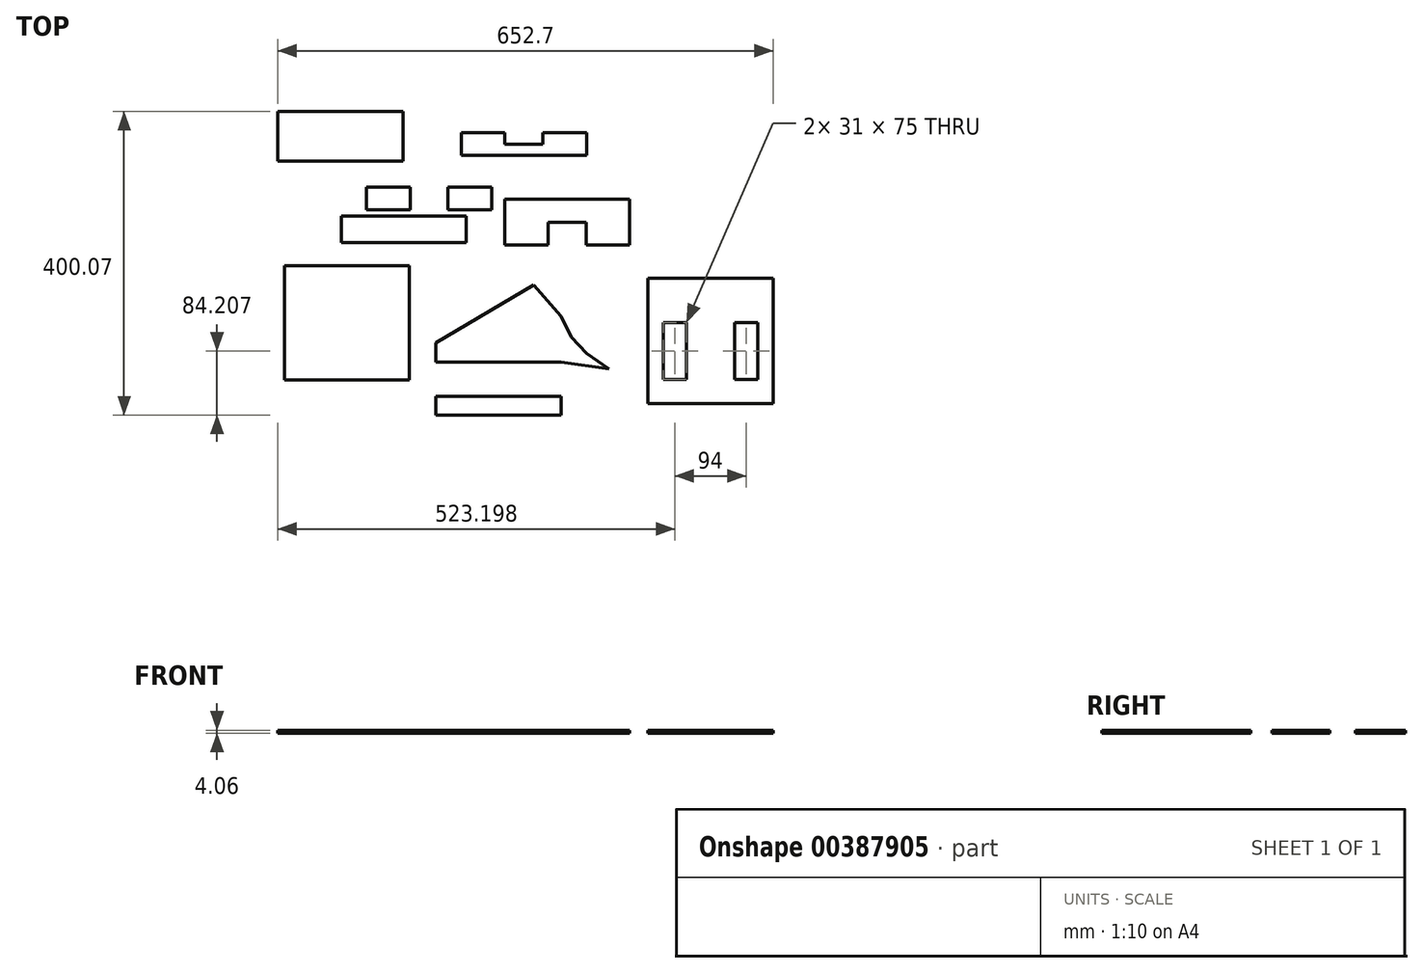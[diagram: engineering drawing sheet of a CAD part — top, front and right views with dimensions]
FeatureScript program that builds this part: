
annotation { "Feature Type Name" : "Feature", "Feature Type Description" : "" }
export const myFeature = defineFeature(function(context is Context, id is Id, definition is map)
    precondition{}
    {
        {
            var Q0;
            Q0=qCreatedBy(makeId("Top.planeOp"),FACE);
            var sketch = newSketch(context, id + "F0", { "sketchPlane" : qUnion([Q0])});
            skLineSegment(sketch, "E0", {"start": v(88.78, 74.8) * mm, "end": v(124.8, 33.23) * mm});
            skLineSegment(sketch, "E1", {"start": v(124.8, 33.23) * mm, "end": v(124.8, -26.77) * mm});
            skLineSegment(sketch, "E2", {"start": v(124.8, -26.77) * mm, "end": v(-40.2, -26.77) * mm});
            skLineSegment(sketch, "E3", {"start": v(88.78, 74.8) * mm, "end": v(-40.2, -1.77) * mm});
            skLineSegment(sketch, "E4", {"start": v(-40.2, -1.77) * mm, "end": v(-40.2, -26.77) * mm});
            skLineSegment(sketch, "E5", {"start": v(124.8, -26.77) * mm, "end": v(187.44, -35.47) * mm});
            skLineSegment(sketch, "E6.bottom", {"start": v(-40.2, -71.68) * mm, "end": v(124.8, -71.68) * mm});
            skLineSegment(sketch, "E6.top", {"start": v(-40.2, -96.68) * mm, "end": v(124.8, -96.68) * mm});
            skLineSegment(sketch, "E6.left", {"start": v(-40.2, -71.68) * mm, "end": v(-40.2, -96.68) * mm});
            skLineSegment(sketch, "E6.right", {"start": v(124.8, -71.68) * mm, "end": v(124.8, -96.68) * mm});
            skLineSegment(sketch, "E7.bottom", {"start": v(-239.93, 99.9) * mm, "end": v(-74.93, 99.9) * mm});
            skLineSegment(sketch, "E7.top", {"start": v(-239.93, -50.1) * mm, "end": v(-74.93, -50.1) * mm});
            skLineSegment(sketch, "E7.left", {"start": v(-239.93, 99.9) * mm, "end": v(-239.93, -50.1) * mm});
            skLineSegment(sketch, "E7.right", {"start": v(-74.93, 99.9) * mm, "end": v(-74.93, -50.1) * mm});
            skLineSegment(sketch, "E8.bottom", {"start": v(239.23, 83.7) * mm, "end": v(404.23, 83.7) * mm});
            skLineSegment(sketch, "E8.top", {"start": v(239.23, -81.3) * mm, "end": v(404.23, -81.3) * mm});
            skLineSegment(sketch, "E8.left", {"start": v(239.23, 83.7) * mm, "end": v(239.23, -81.3) * mm});
            skLineSegment(sketch, "E8.right", {"start": v(404.23, 83.7) * mm, "end": v(404.23, -81.3) * mm});
            skLineSegment(sketch, "E9", {"start": v(124.8, 33.23) * mm, "end": v(138.08, 6.33) * mm});
            skLineSegment(sketch, "E10", {"start": v(138.08, 6.33) * mm, "end": v(158.76, -15.4) * mm});
            skLineSegment(sketch, "E11", {"start": v(158.76, -15.4) * mm, "end": v(187.44, -35.47) * mm});
            skLineSegment(sketch, "E12.bottom", {"start": v(-131.68, 203.81) * mm, "end": v(33.32, 203.81) * mm});
            skLineSegment(sketch, "E12.top", {"start": v(-131.68, 173.81) * mm, "end": v(33.32, 173.81) * mm});
            skLineSegment(sketch, "E12.left", {"start": v(-131.68, 203.81) * mm, "end": v(-131.68, 173.81) * mm});
            skLineSegment(sketch, "E12.right", {"start": v(33.32, 203.81) * mm, "end": v(33.32, 173.81) * mm});
            skLineSegment(sketch, "E13.bottom", {"start": v(-165, 165.7) * mm, "end": v(0, 165.7) * mm});
            skLineSegment(sketch, "E13.top", {"start": v(-165, 130.7) * mm, "end": v(0, 130.7) * mm});
            skLineSegment(sketch, "E13.left", {"start": v(-165, 165.7) * mm, "end": v(-165, 130.7) * mm});
            skLineSegment(sketch, "E13.right", {"start": v(0, 165.7) * mm, "end": v(0, 130.7) * mm});
            skLineSegment(sketch, "E14.bottom", {"start": v(50.31, 187.48) * mm, "end": v(215.31, 187.48) * mm});
            skLineSegment(sketch, "E14.top", {"start": v(50.31, 127.48) * mm, "end": v(215.31, 127.48) * mm});
            skLineSegment(sketch, "E14.left", {"start": v(50.31, 187.48) * mm, "end": v(50.31, 127.48) * mm});
            skLineSegment(sketch, "E14.right", {"start": v(215.31, 187.48) * mm, "end": v(215.31, 127.48) * mm});
            skLineSegment(sketch, "E15.bottom", {"start": v(259.23, 25.03) * mm, "end": v(290.23, 25.03) * mm});
            skLineSegment(sketch, "E15.top", {"start": v(259.23, -49.97) * mm, "end": v(290.23, -49.97) * mm});
            skLineSegment(sketch, "E15.left", {"start": v(259.23, 25.03) * mm, "end": v(259.23, -49.97) * mm});
            skLineSegment(sketch, "E15.right", {"start": v(290.23, 25.03) * mm, "end": v(290.23, -49.97) * mm});
            skLineSegment(sketch, "E16", {"start": v(321.73, 83.7) * mm, "end": v(321.73, -81.3) * mm});
            skLineSegment(sketch, "E17.MirrorCS", {"start": v(384.23, 25.03) * mm, "end": v(353.23, 25.03) * mm});
            skLineSegment(sketch, "E18.MirrorCS", {"start": v(384.23, 25.03) * mm, "end": v(384.23, -49.97) * mm});
            skLineSegment(sketch, "E19.MirrorCS", {"start": v(353.23, 25.03) * mm, "end": v(353.23, -49.97) * mm});
            skLineSegment(sketch, "E20.MirrorCS", {"start": v(384.23, -49.97) * mm, "end": v(353.23, -49.97) * mm});
            skLineSegment(sketch, "E21.bottom", {"start": v(-248.47, 303.39) * mm, "end": v(-83.47, 303.39) * mm});
            skLineSegment(sketch, "E21.top", {"start": v(-248.47, 237.68) * mm, "end": v(-83.47, 237.68) * mm});
            skLineSegment(sketch, "E21.left", {"start": v(-248.47, 303.39) * mm, "end": v(-248.47, 237.68) * mm});
            skLineSegment(sketch, "E21.right", {"start": v(-83.47, 303.39) * mm, "end": v(-83.47, 237.68) * mm});
            skLineSegment(sketch, "E22", {"start": v(-49.18, 173.81) * mm, "end": v(-49.18, 193.81) * mm});
            skLineSegment(sketch, "E23", {"start": v(-49.18, 193.81) * mm, "end": v(-24.18, 193.81) * mm});
            skLineSegment(sketch, "E24", {"start": v(-24.18, 193.81) * mm, "end": v(-24.18, 173.81) * mm});
            skLineSegment(sketch, "E25.MirrorCS", {"start": v(-49.18, 193.81) * mm, "end": v(-74.18, 193.81) * mm});
            skLineSegment(sketch, "E26.MirrorCS", {"start": v(-74.18, 193.81) * mm, "end": v(-74.18, 173.81) * mm});
            skLineSegment(sketch, "E27", {"start": v(-82.5, 165.7) * mm, "end": v(-82.5, 130.7) * mm});
            skLineSegment(sketch, "E28", {"start": v(-107.5, 165.7) * mm, "end": v(-107.5, 150.7) * mm});
            skLineSegment(sketch, "E29", {"start": v(-107.5, 150.7) * mm, "end": v(-82.5, 150.7) * mm});
            skLineSegment(sketch, "E30.MirrorCS", {"start": v(-57.5, 150.7) * mm, "end": v(-82.5, 150.7) * mm});
            skLineSegment(sketch, "E31.MirrorCS", {"start": v(-57.5, 165.7) * mm, "end": v(-57.5, 150.7) * mm});
            skLineSegment(sketch, "E32.bottom", {"start": v(-6.75, 275.29) * mm, "end": v(158.25, 275.29) * mm});
            skLineSegment(sketch, "E32.top", {"start": v(-6.75, 245.29) * mm, "end": v(158.25, 245.29) * mm});
            skLineSegment(sketch, "E32.left", {"start": v(-6.75, 275.29) * mm, "end": v(-6.75, 245.29) * mm});
            skLineSegment(sketch, "E32.right", {"start": v(158.25, 275.29) * mm, "end": v(158.25, 245.29) * mm});
            skLineSegment(sketch, "E33", {"start": v(75.75, 245.29) * mm, "end": v(75.75, 275.29) * mm});
            skLineSegment(sketch, "E34", {"start": v(50.75, 245.29) * mm, "end": v(50.75, 275.29) * mm});
            skLineSegment(sketch, "E35.MirrorCS", {"start": v(100.75, 245.29) * mm, "end": v(100.75, 275.29) * mm});
            skLineSegment(sketch, "E36", {"start": v(-74.18, 193.81) * mm, "end": v(-74.18, 203.81) * mm});
            skLineSegment(sketch, "E37", {"start": v(-49.18, 193.81) * mm, "end": v(-49.18, 203.81) * mm});
            skLineSegment(sketch, "E38", {"start": v(-24.18, 193.81) * mm, "end": v(-24.18, 203.81) * mm});
            skLineSegment(sketch, "E39", {"start": v(132.81, 127.48) * mm, "end": v(132.81, 187.48) * mm});
            skLineSegment(sketch, "E40", {"start": v(132.81, 157.48) * mm, "end": v(157.81, 157.48) * mm});
            skLineSegment(sketch, "E41", {"start": v(157.81, 157.48) * mm, "end": v(157.81, 127.48) * mm});
            skLineSegment(sketch, "E42.MirrorCS", {"start": v(132.81, 157.48) * mm, "end": v(107.81, 157.48) * mm});
            skLineSegment(sketch, "E43.MirrorCS", {"start": v(107.81, 157.48) * mm, "end": v(107.81, 127.48) * mm});
            skLineSegment(sketch, "E44", {"start": v(50.75, 260.29) * mm, "end": v(100.75, 260.29) * mm});
            skSolve(sketch);
        }
        {
            var Q0;
            Q0=makeQuery(id+"F0.imprint","IMPRINT",FACE,{"disambiguationData":[TD([[makeQuery(id+"F0.imprint","IMPRINT",EDGE,{"derivedFrom":sQuery(id+"F0.wireOp",EDGE,"E0")}),-1.0]])]});
            var Q1;
            Q1=makeQuery(id+"F0.imprint","IMPRINT",FACE,{"disambiguationData":[TD([[makeQuery(id+"F0.imprint","IMPRINT",EDGE,{"derivedFrom":sQuery(id+"F0.wireOp",EDGE,"E6.bottom")}),-1.0]])]});
            var Q2;
            Q2=makeQuery(id+"F0.imprint","IMPRINT",FACE,{"disambiguationData":[TD([[makeQuery(id+"F0.imprint","IMPRINT",EDGE,{"derivedFrom":sQuery(id+"F0.wireOp",EDGE,"E1")}),1.0]])]});
            var Q3;
            {var subQ4=sQuery(id+"F0.wireOp",EDGE,"E14.left");Q3=makeQuery(id+"F0.imprint","IMPRINT",FACE,{"disambiguationData":[TD([[makeQuery(id+"F0.imprint","IMPRINT",EDGE,{"derivedFrom":subQ4}),1.0]])]});}
            var Q4;
            {var subQ4=sQuery(id+"F0.wireOp",EDGE,"E14.right");Q4=makeQuery(id+"F0.imprint","IMPRINT",FACE,{"disambiguationData":[TD([[makeQuery(id+"F0.imprint","IMPRINT",EDGE,{"derivedFrom":subQ4}),-1.0]])]});}
            var Q5;
            Q5=makeQuery(id+"F0.imprint","IMPRINT",FACE,{"disambiguationData":[TD([[makeQuery(id+"F0.imprint","IMPRINT",EDGE,{"derivedFrom":sQuery(id+"F0.wireOp",EDGE,"E7.bottom")}),-1.0]])]});
            var Q6;
            {var subQ0=sQuery(id+"F0.wireOp",EDGE,"E8.left");Q6=makeQuery(id+"F0.imprint","IMPRINT",FACE,{"disambiguationData":[TD([[makeQuery(id+"F0.imprint","IMPRINT",EDGE,{"derivedFrom":subQ0}),1.0]])]});}
            var Q7;
            {var subQ1=sQuery(id+"F0.wireOp",EDGE,"E8.right");Q7=makeQuery(id+"F0.imprint","IMPRINT",FACE,{"disambiguationData":[TD([[makeQuery(id+"F0.imprint","IMPRINT",EDGE,{"derivedFrom":subQ1}),-1.0]])]});}
            var Q8;
            Q8=makeQuery(id+"F0.imprint","IMPRINT",FACE,{"disambiguationData":[TD([[makeQuery(id+"F0.imprint","IMPRINT",EDGE,{"derivedFrom":sQuery(id+"F0.wireOp",EDGE,"E21.bottom")}),-1.0]])]});
            var Q9;
            {var subQ0=sQuery(id+"F0.wireOp",EDGE,"E13.right");Q9=makeQuery(id+"F0.imprint","IMPRINT",FACE,{"disambiguationData":[TD([[makeQuery(id+"F0.imprint","IMPRINT",EDGE,{"derivedFrom":subQ0}),-1.0]])]});}
            var Q10;
            {var subQ0=sQuery(id+"F0.wireOp",EDGE,"E13.left");Q10=makeQuery(id+"F0.imprint","IMPRINT",FACE,{"disambiguationData":[TD([[makeQuery(id+"F0.imprint","IMPRINT",EDGE,{"derivedFrom":subQ0}),1.0]])]});}
            var Q11;
            {var subQ0=sQuery(id+"F0.wireOp",EDGE,"E32.left");Q11=makeQuery(id+"F0.imprint","IMPRINT",FACE,{"disambiguationData":[TD([[makeQuery(id+"F0.imprint","IMPRINT",EDGE,{"derivedFrom":subQ0}),1.0]])]});}
            var Q12;
            {var subQ0=sQuery(id+"F0.wireOp",EDGE,"E32.right");Q12=makeQuery(id+"F0.imprint","IMPRINT",FACE,{"disambiguationData":[TD([[makeQuery(id+"F0.imprint","IMPRINT",EDGE,{"derivedFrom":subQ0}),-1.0]])]});}
            var Q13;
            {var subQ3=sQuery(id+"F0.wireOp",EDGE,"E28");Q13=makeQuery(id+"F0.imprint","IMPRINT",FACE,{"disambiguationData":[TD([[makeQuery(id+"F0.imprint","IMPRINT",EDGE,{"derivedFrom":subQ3}),1.0]])]});}
            var Q14;
            {var subQ4=sQuery(id+"F0.wireOp",EDGE,"E30.MirrorCS");Q14=makeQuery(id+"F0.imprint","IMPRINT",FACE,{"disambiguationData":[TD([[makeQuery(id+"F0.imprint","IMPRINT",EDGE,{"derivedFrom":subQ4}),-1.0]])]});}
            var Q15;
            {var subQ1=sQuery(id+"F0.wireOp",EDGE,"E12.left");Q15=makeQuery(id+"F0.imprint","IMPRINT",FACE,{"disambiguationData":[TD([[makeQuery(id+"F0.imprint","IMPRINT",EDGE,{"derivedFrom":subQ1}),1.0]])]});}
            var Q16;
            {var subQ1=sQuery(id+"F0.wireOp",EDGE,"E12.right");Q16=makeQuery(id+"F0.imprint","IMPRINT",FACE,{"disambiguationData":[TD([[makeQuery(id+"F0.imprint","IMPRINT",EDGE,{"derivedFrom":subQ1}),-1.0]])]});}
            var Q17;
            {var subQ0=sQuery(id+"F0.wireOp",EDGE,"E33");var subQ1=sQuery(id+"F0.wireOp",EDGE,"E32.top");var subQ2=makeQuery(id+"F0.imprint","INTERSECT",VERTEX,{"derivedFrom":[subQ1,subQ0]});Q17=makeQuery(id+"F0.imprint","IMPRINT",FACE,{"disambiguationData":[TD([[makeQuery(id+"F0.imprint","IMPRINT",EDGE,{"disambiguationData":[TD([[subQ2,1.0]])],"derivedFrom":subQ1}),1.0]])]});}
            var Q18;
            {var subQ0=sQuery(id+"F0.wireOp",EDGE,"E33");var subQ1=sQuery(id+"F0.wireOp",EDGE,"E32.top");var subQ2=makeQuery(id+"F0.imprint","INTERSECT",VERTEX,{"derivedFrom":[subQ1,subQ0]});Q18=makeQuery(id+"F0.imprint","IMPRINT",FACE,{"disambiguationData":[TD([[makeQuery(id+"F0.imprint","IMPRINT",EDGE,{"disambiguationData":[TD([[subQ2,-1.0]])],"derivedFrom":subQ1}),1.0]])]});}
            extrude(context, id + "F1", {"entities" : qUnion([Q0, Q1, Q2, Q3, Q4, Q5, Q6, Q7, Q8, Q9, Q10, Q11, Q12, Q13, Q14, Q15, Q16, Q17, Q18]), "depth" : 4.06 * mm});
        }
    });
